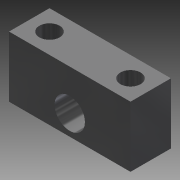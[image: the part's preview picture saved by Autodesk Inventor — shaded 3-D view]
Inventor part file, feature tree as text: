
AUTODESK INVENTOR PART (.ipt)
format: ipt  version: 2012 (Build 160160000, 160)  size: 93,184 bytes
history: native  units: in
note: dims shown in document units (in); Inventor stores cm internally (conversion verified against a paired STEP export)
features: extrude x2, sketch x2
ambient origin geometry x8: Origin, YZ Plane, XZ Plane, XY Plane, X Axis, Y Axis, Z Axis, Center Point
bodies: Solid1 (feature_tree)
feature tree (4):
  extrude  "Extrusion1"  Depth=1.5in
  extrude  "Extrusion2"  Depth=0.5in TaperAngle=0.0deg
  sketch  "Sketch1"  dims[d0=0.75in d1=1.5in]
  sketch  "Sketch2"  dims[d2=0.375in d3=0.5in d4=0.0in d5=0.25in d6=0.25in d7=0.25in d8=0.25in d9=0.25in d10=0.5in d11=0.0in]
